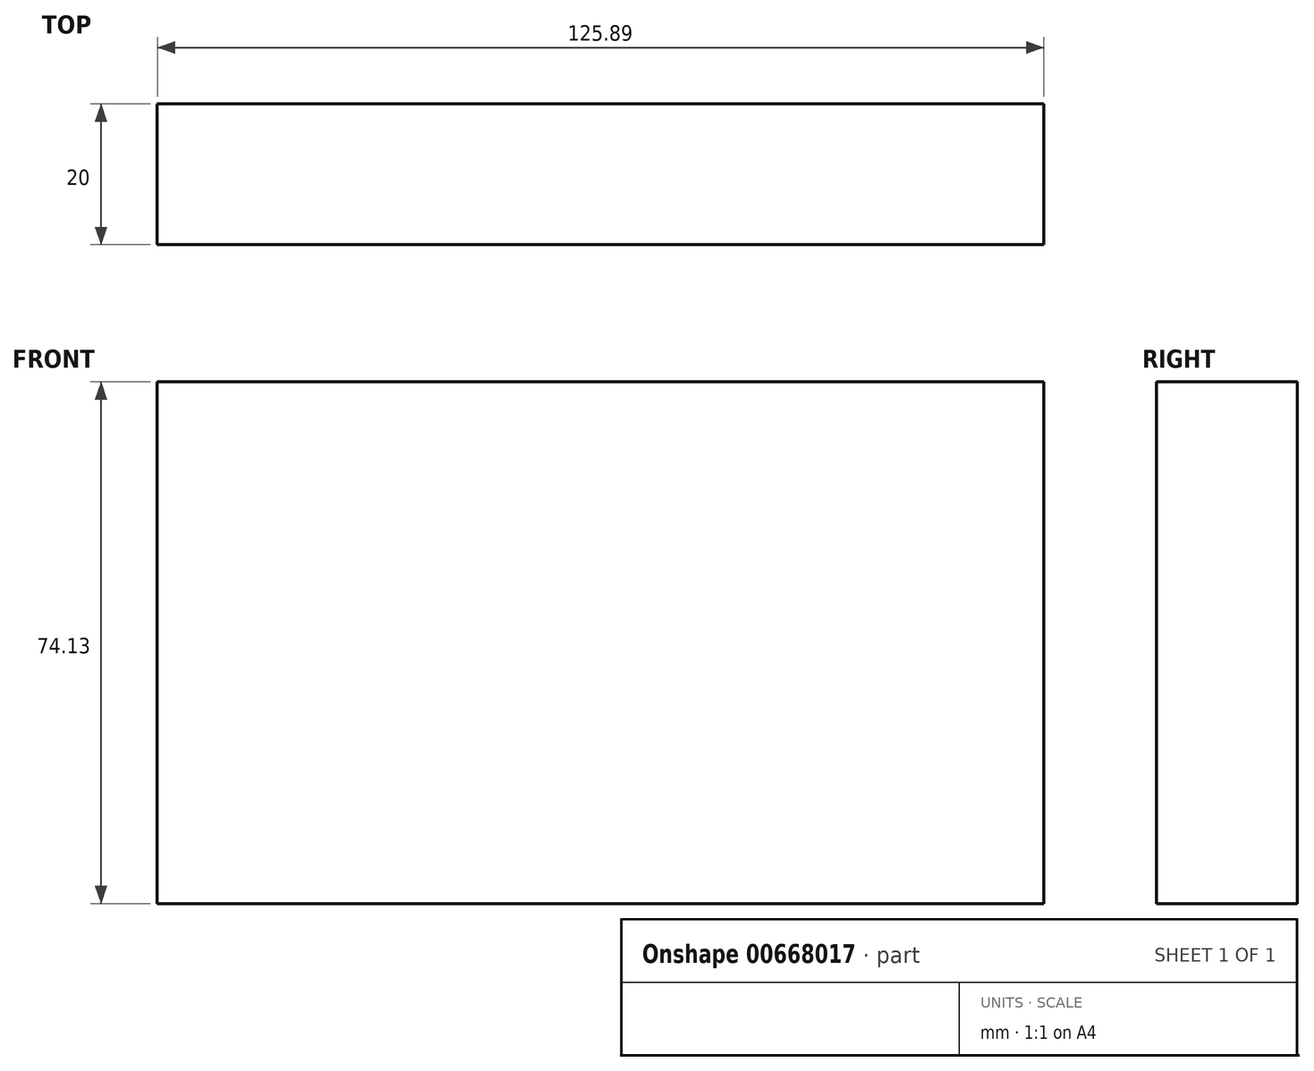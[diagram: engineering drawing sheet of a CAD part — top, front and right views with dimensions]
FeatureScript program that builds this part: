
annotation { "Feature Type Name" : "Feature", "Feature Type Description" : "" }
export const myFeature = defineFeature(function(context is Context, id is Id, definition is map)
    precondition{}
    {
        {
            var Q0;
            Q0=qCreatedBy(makeId("Front.planeOp"),FACE);
            var sketch = newSketch(context, id + "F0", { "sketchPlane" : qUnion([Q0])});
            skLineSegment(sketch, "E0.bottom", {"start": v(-60.16, 41.44) * mm, "end": v(65.73, 41.44) * mm});
            skLineSegment(sketch, "E0.top", {"start": v(-60.16, -32.69) * mm, "end": v(65.73, -32.69) * mm});
            skLineSegment(sketch, "E0.left", {"start": v(-60.16, 41.44) * mm, "end": v(-60.16, -32.69) * mm});
            skLineSegment(sketch, "E0.right", {"start": v(65.73, 41.44) * mm, "end": v(65.73, -32.69) * mm});
            skLineSegment(sketch, "E1.bottom", {"start": v(-6.5, -33.83) * mm, "end": v(-29.26, -33.83) * mm});
            skLineSegment(sketch, "E1.top", {"start": v(-6.5, -64.54) * mm, "end": v(-29.26, -64.54) * mm});
            skLineSegment(sketch, "E1.left", {"start": v(-6.5, -33.83) * mm, "end": v(-6.5, -64.54) * mm});
            skLineSegment(sketch, "E1.right", {"start": v(-29.26, -33.83) * mm, "end": v(-29.26, -64.54) * mm});
            skSolve(sketch);
        }
        {
            var Q0;
            Q0=makeQuery(id+"F0.imprint","IMPRINT",FACE,{"disambiguationData":[TD([[makeQuery(id+"F0.imprint","IMPRINT",EDGE,{"derivedFrom":sQuery(id+"F0.wireOp",EDGE,"E0.bottom")}),-1.0]])]});
            extrude(context, id + "F1", {"entities" : qUnion([Q0]), "depth" : 20 * mm, "offsetDistance" : 25.4 * mm});
        }
    });
